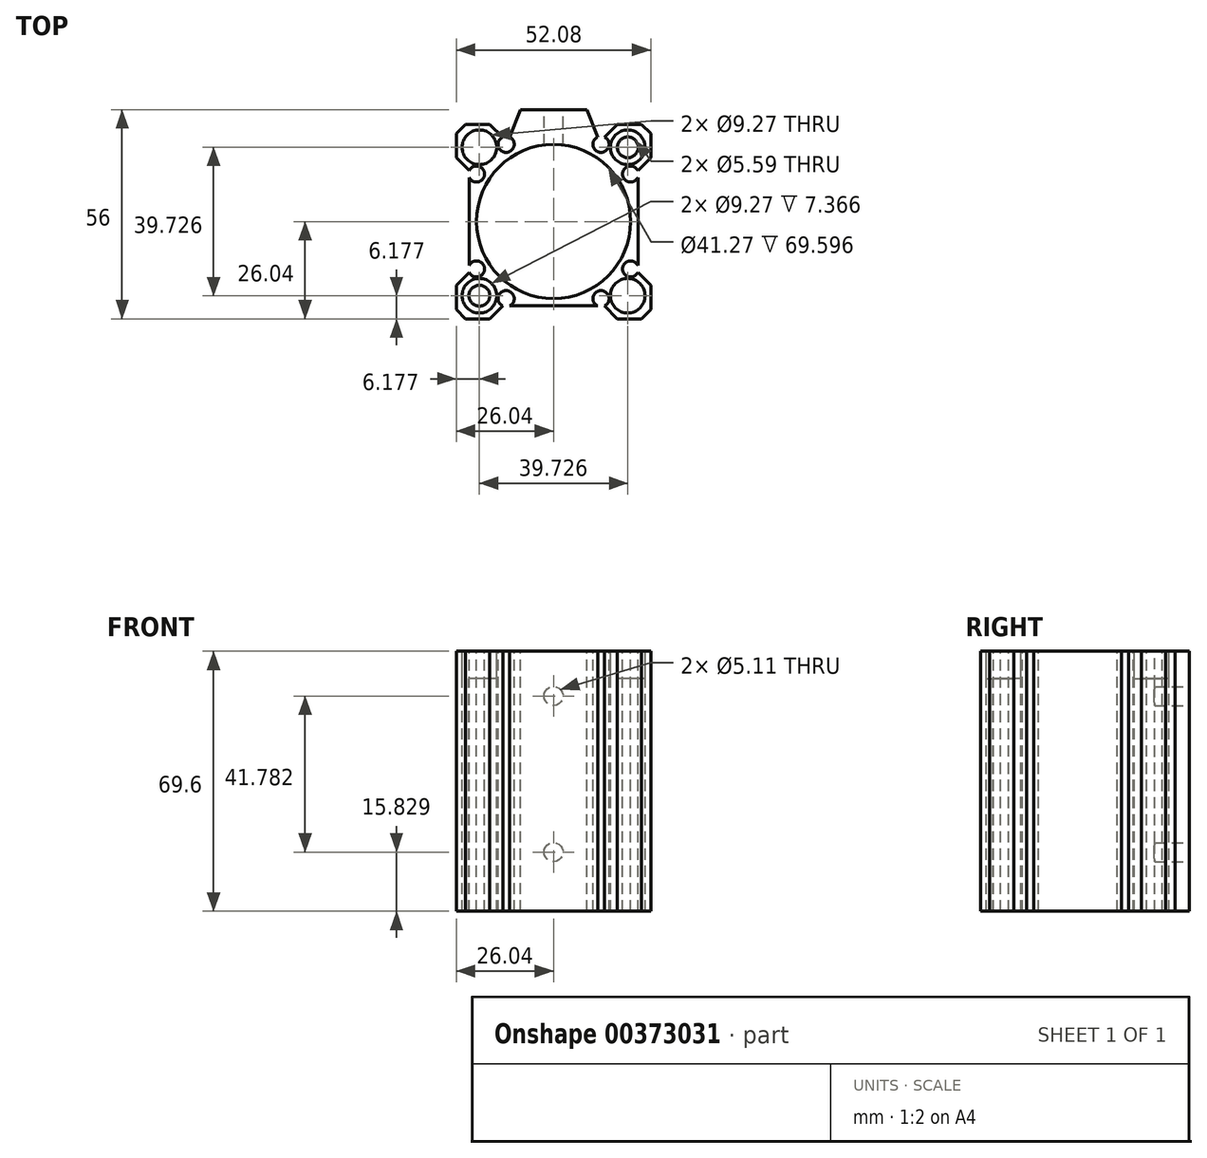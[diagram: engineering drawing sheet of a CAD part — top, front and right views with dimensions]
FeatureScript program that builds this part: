
annotation { "Feature Type Name" : "Feature", "Feature Type Description" : "" }
export const myFeature = defineFeature(function(context is Context, id is Id, definition is map)
    precondition{}
    {
        {
            var Q0;
            Q0=qCreatedBy(makeId("Top.planeOp"),FACE);
            var sketch = newSketch(context, id + "F0", { "sketchPlane" : qUnion([Q0])});
            skLineSegment(sketch, "E0.bottom", {"start": v(23.56, 26.03) * mm, "end": v(17.05, 26.03) * mm});
            skLineSegment(sketch, "E0.top", {"start": v(23.56, -26.04) * mm, "end": v(17.05, -26.04) * mm});
            skLineSegment(sketch, "E0.left", {"start": v(26.04, 23.56) * mm, "end": v(26.04, 17.05) * mm});
            skLineSegment(sketch, "E0.right", {"start": v(-26.04, 23.56) * mm, "end": v(-26.04, 17.05) * mm});
            skPoint(sketch, "E0.middle", {"position": v(0, 0) * mm});
            skLineSegment(sketch, "E1.0", {"start": v(-26.04, 17.05) * mm, "end": v(-22.6, 13.61) * mm});
            skLineSegment(sketch, "E2.0", {"start": v(-17.05, 26.04) * mm, "end": v(-13.61, 22.6) * mm});
            skLineSegment(sketch, "E3.0", {"start": v(17.05, 26.03) * mm, "end": v(13.61, 22.6) * mm});
            skLineSegment(sketch, "E4.0", {"start": v(26.04, 17.05) * mm, "end": v(22.6, 13.61) * mm});
            skCircle(sketch, "E5", {"center": v(19.86, 19.86) * mm, "radius": 4.64 * mm});
            skCircle(sketch, "E6.MirrorC", {"center": v(19.86, -19.86) * mm, "radius": 4.64 * mm});
            skCircle(sketch, "E7.MirrorC", {"center": v(-19.86, 19.86) * mm, "radius": 4.64 * mm});
            skCircle(sketch, "E8.MirrorC", {"center": v(-19.86, -19.86) * mm, "radius": 4.64 * mm});
            skLineSegment(sketch, "E9", {"start": v(0, 22.6) * mm, "end": v(0, 0) * mm});
            skArc(sketch, "E10", {"start": v(11.79, 22.6) * mm, "mid": v(12.7, 18.48) * mm, "end": v(13.61, 22.6) * mm});
            skArc(sketch, "E11", {"start": v(22.6, 13.61) * mm, "mid": v(18.48, 12.7) * mm, "end": v(22.6, 11.79) * mm});
            skArc(sketch, "E12.MirrorC", {"start": v(22.6, -13.61) * mm, "mid": v(18.48, -12.7) * mm, "end": v(22.6, -11.79) * mm});
            skArc(sketch, "E13.MirrorC", {"start": v(11.79, -22.6) * mm, "mid": v(12.7, -18.48) * mm, "end": v(13.61, -22.6) * mm});
            skArc(sketch, "E14.MirrorC", {"start": v(-11.79, 22.6) * mm, "mid": v(-12.7, 18.48) * mm, "end": v(-13.61, 22.6) * mm});
            skArc(sketch, "E15.MirrorC", {"start": v(-22.6, 13.61) * mm, "mid": v(-18.48, 12.7) * mm, "end": v(-22.6, 11.79) * mm});
            skArc(sketch, "E16.MirrorC", {"start": v(-22.6, -13.61) * mm, "mid": v(-18.48, -12.7) * mm, "end": v(-22.6, -11.79) * mm});
            skArc(sketch, "E17.MirrorC", {"start": v(-11.79, -22.6) * mm, "mid": v(-12.7, -18.48) * mm, "end": v(-13.61, -22.6) * mm});
            skLineSegment(sketch, "E18", {"start": v(-23.56, 26.03) * mm, "end": v(-26.04, 23.56) * mm});
            skLineSegment(sketch, "E19", {"start": v(23.56, 26.03) * mm, "end": v(26.04, 23.56) * mm});
            skLineSegment(sketch, "E20", {"start": v(26.04, -23.56) * mm, "end": v(23.56, -26.03) * mm});
            skLineSegment(sketch, "E21", {"start": v(-23.56, -26.03) * mm, "end": v(-26.04, -23.56) * mm});
            skPoint(sketch, "E22.orphan", {"position": v(-26.04, -26.03) * mm});
            skPoint(sketch, "E23.orphan", {"position": v(26.03, -26.04) * mm});
            skPoint(sketch, "E24.orphan", {"position": v(26.04, 26.04) * mm});
            skPoint(sketch, "E25.orphan", {"position": v(-26.04, 26.04) * mm});
            skLineSegment(sketch, "E26.trimOffspring", {"start": v(26.04, -17.05) * mm, "end": v(26.04, -23.56) * mm});
            skLineSegment(sketch, "E27.trimOffspring", {"start": v(-17.05, 26.03) * mm, "end": v(-23.56, 26.03) * mm});
            skPoint(sketch, "E28.orphan", {"position": v(12.7, 26.03) * mm});
            skPoint(sketch, "E29.orphan", {"position": v(-12.7, 26.03) * mm});
            skLineSegment(sketch, "E30.trimOffspring", {"start": v(22.6, -13.61) * mm, "end": v(26.04, -17.05) * mm});
            skLineSegment(sketch, "E31.trimOffspring", {"start": v(13.61, -22.6) * mm, "end": v(17.05, -26.04) * mm});
            skLineSegment(sketch, "E32.trimOffspring", {"start": v(-17.05, -26.04) * mm, "end": v(-23.56, -26.04) * mm});
            skLineSegment(sketch, "E33.trimOffspring", {"start": v(-13.61, -22.6) * mm, "end": v(-17.05, -26.03) * mm});
            skLineSegment(sketch, "E34.trimOffspring", {"start": v(-26.04, -17.05) * mm, "end": v(-26.04, -23.56) * mm});
            skLineSegment(sketch, "E35.trimOffspring", {"start": v(-22.6, -13.61) * mm, "end": v(-26.03, -17.05) * mm});
            skLineSegment(sketch, "E36", {"start": v(-11.79, 22.6) * mm, "end": v(11.79, 22.6) * mm});
            skLineSegment(sketch, "E37", {"start": v(22.6, 11.79) * mm, "end": v(22.6, -11.79) * mm});
            skLineSegment(sketch, "E38", {"start": v(11.79, -22.6) * mm, "end": v(-11.79, -22.6) * mm});
            skLineSegment(sketch, "E39", {"start": v(-22.6, -11.79) * mm, "end": v(-22.6, 11.79) * mm});
            skPoint(sketch, "E40.start.orphan", {"position": v(-26.04, 0) * mm});
            skLineSegment(sketch, "E41.trimOffspring", {"start": v(0, 0) * mm, "end": v(26.04, 0) * mm});
            skPoint(sketch, "E42.trimOffspring.end.orphan", {"position": v(0, -26.03) * mm});
            skCircle(sketch, "E43", {"center": v(0, 0) * mm, "radius": 20.83 * mm});
            skLineSegment(sketch, "E44.0", {"start": v(-8.9, 29.96) * mm, "end": v(8.89, 29.96) * mm});
            skLineSegment(sketch, "E45", {"start": v(0, 26.03) * mm, "end": v(0, 22.6) * mm});
            skLineSegment(sketch, "E46.0", {"start": v(-8.9, 29.96) * mm, "end": v(-8.9, 29.37) * mm});
            skLineSegment(sketch, "E47", {"start": v(-11.79, 22.6) * mm, "end": v(-8.9, 29.96) * mm});
            skLineSegment(sketch, "E48", {"start": v(8.89, 29.96) * mm, "end": v(11.79, 22.6) * mm});
            skPoint(sketch, "E49.orphan", {"position": v(-11.79, 29.96) * mm});
            skPoint(sketch, "E50.orphan", {"position": v(11.79, 29.96) * mm});
            skPoint(sketch, "E51.orphan", {"position": v(0, 29.96) * mm});
            skSolve(sketch);
        }
        {
            var Q0;
            Q0=makeQuery(id+"F0.imprint","IMPRINT",FACE,{"disambiguationData":[TD([[makeQuery(id+"F0.imprint","IMPRINT",EDGE,{"derivedFrom":sQuery(id+"F0.wireOp",EDGE,"E0.top")}),-1.0]])]});
            var Q1;
            Q1=makeQuery(id+"F0.imprint","IMPRINT",FACE,{"disambiguationData":[TD([[makeQuery(id+"F0.imprint","IMPRINT",EDGE,{"derivedFrom":sQuery(id+"F0.wireOp",EDGE,"E44.0")}),-1.0]])]});
            var Q2;
            Q2=makeQuery(id+"F0.imprint","IMPRINT",FACE,{"disambiguationData":[TD([[makeQuery(id+"F0.imprint","IMPRINT",EDGE,{"derivedFrom":sQuery(id+"F0.wireOp",EDGE,"E0.bottom")}),1.0]])]});
            var Q3;
            Q3=makeQuery(id+"F0.imprint","IMPRINT",FACE,{"disambiguationData":[TD([[makeQuery(id+"F0.imprint","IMPRINT",EDGE,{"derivedFrom":sQuery(id+"F0.wireOp",EDGE,"E6.MirrorC")}),-1.0]])]});
            var Q4;
            Q4=makeQuery(id+"F0.imprint","IMPRINT",FACE,{"disambiguationData":[TD([[makeQuery(id+"F0.imprint","IMPRINT",EDGE,{"derivedFrom":sQuery(id+"F0.wireOp",EDGE,"E5")}),1.0]])]});
            var Q5;
            Q5=makeQuery(id+"F0.imprint","IMPRINT",FACE,{"disambiguationData":[TD([[makeQuery(id+"F0.imprint","IMPRINT",EDGE,{"derivedFrom":sQuery(id+"F0.wireOp",EDGE,"E7.MirrorC")}),-1.0]])]});
            var Q6;
            Q6=makeQuery(id+"F0.imprint","IMPRINT",FACE,{"disambiguationData":[TD([[makeQuery(id+"F0.imprint","IMPRINT",EDGE,{"derivedFrom":sQuery(id+"F0.wireOp",EDGE,"E8.MirrorC")}),1.0]])]});
            var Q7;
            {var subQ0=sQuery(id+"F0.wireOp",EDGE,"E41.trimOffspring");var subQ1=sQuery(id+"F0.wireOp",EDGE,"E9");var subQ2=makeQuery(id+"F0.imprint","INTERSECT",VERTEX,{"derivedFrom":[subQ1,subQ0]});Q7=makeQuery(id+"F0.imprint","IMPRINT",FACE,{"disambiguationData":[TD([[makeQuery(id+"F0.imprint","IMPRINT",EDGE,{"disambiguationData":[TD([[subQ2,1.0]])],"derivedFrom":subQ1}),1.0]])]});}
            var Q8;
            {var subQ0=sQuery(id+"F0.wireOp",EDGE,"E41.trimOffspring");var subQ1=sQuery(id+"F0.wireOp",EDGE,"E9");var subQ2=makeQuery(id+"F0.imprint","INTERSECT",VERTEX,{"derivedFrom":[subQ1,subQ0]});Q8=makeQuery(id+"F0.imprint","IMPRINT",FACE,{"disambiguationData":[TD([[makeQuery(id+"F0.imprint","IMPRINT",EDGE,{"disambiguationData":[TD([[subQ2,1.0]])],"derivedFrom":subQ1}),-1.0]])]});}
            extrude(context, id + "F1", {"entities" : qUnion([Q0, Q1, Q2, Q3, Q4, Q5, Q6, Q7, Q8]), "oppositeDirection" : true, "depth" : 69.6 * mm, "offsetDistance" : 25.4 * mm});
        }
        {
            var Q0;
            Q0=sQuery(id+"F0.wireOp",VERTEX,"E7.MirrorC.center");
            var Q1;
            Q1=sQuery(id+"F0.wireOp",VERTEX,"E5.center");
            var Q2;
            Q2=sQuery(id+"F0.wireOp",VERTEX,"E6.MirrorC.center");
            var Q3;
            Q3=sQuery(id+"F0.wireOp",VERTEX,"E8.MirrorC.center");
            var Q4;
            Q4=makeQuery(id+"F1.opExtrude","SWEPT_BODY",BODY,{"disambiguationData":[OSD([sQuery(id+"F0.wireOp",EDGE,"E0.bottom"),sQuery(id+"F0.wireOp",EDGE,"E0.top"),sQuery(id+"F0.wireOp",EDGE,"E0.left"),sQuery(id+"F0.wireOp",EDGE,"E0.right"),sQuery(id+"F0.wireOp",EDGE,"E1.0"),sQuery(id+"F0.wireOp",EDGE,"E2.0"),sQuery(id+"F0.wireOp",EDGE,"E3.0"),sQuery(id+"F0.wireOp",EDGE,"E4.0"),sQuery(id+"F0.wireOp",EDGE,"E10"),sQuery(id+"F0.wireOp",EDGE,"E11"),sQuery(id+"F0.wireOp",EDGE,"E12.MirrorC"),sQuery(id+"F0.wireOp",EDGE,"E13.MirrorC"),sQuery(id+"F0.wireOp",EDGE,"E14.MirrorC"),sQuery(id+"F0.wireOp",EDGE,"E15.MirrorC"),sQuery(id+"F0.wireOp",EDGE,"E16.MirrorC"),sQuery(id+"F0.wireOp",EDGE,"E17.MirrorC"),sQuery(id+"F0.wireOp",EDGE,"E18"),sQuery(id+"F0.wireOp",EDGE,"E19"),sQuery(id+"F0.wireOp",EDGE,"E20"),sQuery(id+"F0.wireOp",EDGE,"E21"),sQuery(id+"F0.wireOp",EDGE,"E26.trimOffspring"),sQuery(id+"F0.wireOp",EDGE,"E27.trimOffspring"),sQuery(id+"F0.wireOp",EDGE,"E30.trimOffspring"),sQuery(id+"F0.wireOp",EDGE,"E31.trimOffspring"),sQuery(id+"F0.wireOp",EDGE,"E32.trimOffspring"),sQuery(id+"F0.wireOp",EDGE,"E33.trimOffspring"),sQuery(id+"F0.wireOp",EDGE,"E34.trimOffspring"),sQuery(id+"F0.wireOp",EDGE,"E35.trimOffspring"),sQuery(id+"F0.wireOp",EDGE,"E37"),sQuery(id+"F0.wireOp",EDGE,"E38"),sQuery(id+"F0.wireOp",EDGE,"E39"),sQuery(id+"F0.wireOp",EDGE,"E44.0"),sQuery(id+"F0.wireOp",EDGE,"E47"),sQuery(id+"F0.wireOp",EDGE,"E48")])]});
            hole(context, id + "F2", {"style" : HoleStyle.C_BORE, "endStyle" : HoleEndStyle.THROUGH, "holeDiameter" : 5.6 * mm, "cBoreDiameter" : 9.27 * mm, "cBoreDepth" : 7.37 * mm, "majorDiameter" : 6.35 * mm, "isTappedThrough" : true, "tappedDepth" : 13.2 * mm, "tapClearance" : 3, "startFromSketch" : true, "locations" : qUnion([Q0, Q1, Q2, Q3]), "scope" : qUnion([Q4])});
        }
        {
            var Q0;
            Q0=sQuery(id+"F0.wireOp",VERTEX,"E0.middle");
            var Q1;
            Q1=makeQuery(id+"F1.opExtrude","SWEPT_BODY",BODY,{"disambiguationData":[OSD([sQuery(id+"F0.wireOp",EDGE,"E0.bottom"),sQuery(id+"F0.wireOp",EDGE,"E0.top"),sQuery(id+"F0.wireOp",EDGE,"E0.left"),sQuery(id+"F0.wireOp",EDGE,"E0.right"),sQuery(id+"F0.wireOp",EDGE,"E1.0"),sQuery(id+"F0.wireOp",EDGE,"E2.0"),sQuery(id+"F0.wireOp",EDGE,"E3.0"),sQuery(id+"F0.wireOp",EDGE,"E4.0"),sQuery(id+"F0.wireOp",EDGE,"E10"),sQuery(id+"F0.wireOp",EDGE,"E11"),sQuery(id+"F0.wireOp",EDGE,"E12.MirrorC"),sQuery(id+"F0.wireOp",EDGE,"E13.MirrorC"),sQuery(id+"F0.wireOp",EDGE,"E14.MirrorC"),sQuery(id+"F0.wireOp",EDGE,"E15.MirrorC"),sQuery(id+"F0.wireOp",EDGE,"E16.MirrorC"),sQuery(id+"F0.wireOp",EDGE,"E17.MirrorC"),sQuery(id+"F0.wireOp",EDGE,"E18"),sQuery(id+"F0.wireOp",EDGE,"E19"),sQuery(id+"F0.wireOp",EDGE,"E20"),sQuery(id+"F0.wireOp",EDGE,"E21"),sQuery(id+"F0.wireOp",EDGE,"E26.trimOffspring"),sQuery(id+"F0.wireOp",EDGE,"E27.trimOffspring"),sQuery(id+"F0.wireOp",EDGE,"E30.trimOffspring"),sQuery(id+"F0.wireOp",EDGE,"E31.trimOffspring"),sQuery(id+"F0.wireOp",EDGE,"E32.trimOffspring"),sQuery(id+"F0.wireOp",EDGE,"E33.trimOffspring"),sQuery(id+"F0.wireOp",EDGE,"E34.trimOffspring"),sQuery(id+"F0.wireOp",EDGE,"E35.trimOffspring"),sQuery(id+"F0.wireOp",EDGE,"E37"),sQuery(id+"F0.wireOp",EDGE,"E38"),sQuery(id+"F0.wireOp",EDGE,"E39"),sQuery(id+"F0.wireOp",EDGE,"E44.0"),sQuery(id+"F0.wireOp",EDGE,"E47"),sQuery(id+"F0.wireOp",EDGE,"E48")])]});
            hole(context, id + "F3", {"style" : HoleStyle.SIMPLE, "endStyle" : HoleEndStyle.THROUGH, "holeDiameter" : 41.27 * mm, "majorDiameter" : 6.35 * mm, "isTappedThrough" : true, "tappedDepth" : 13.2 * mm, "tapClearance" : 3, "startFromSketch" : true, "locations" : qUnion([Q0]), "scope" : qUnion([Q1])});
        }
        {
            var Q0;
            Q0=makeQuery(id+"F1.opExtrude","SWEPT_FACE",FACE,{"disambiguationData":[OSD([sQuery(id+"F0.wireOp",EDGE,"E44.0")])]});
            var sketch = newSketch(context, id + "F4", { "sketchPlane" : qUnion([Q0])});
            skLineSegment(sketch, "E52", {"start": v(0, 0) * mm, "end": v(0, -69.6) * mm});
            skLineSegment(sketch, "E53", {"start": v(-10.34, -11.99) * mm, "end": v(11.12, -11.99) * mm});
            skLineSegment(sketch, "E54", {"start": v(-10.46, -53.77) * mm, "end": v(11.12, -53.77) * mm});
            skPoint(sketch, "E55", {"position": v(0, -11.99) * mm});
            skPoint(sketch, "E56", {"position": v(0, -53.77) * mm});
            skSolve(sketch);
        }
        {
            var Q0;
            Q0=sQuery(id+"F4.wireOp",VERTEX,"E55");
            var Q1;
            Q1=sQuery(id+"F4.wireOp",VERTEX,"E56");
            var Q2;
            Q2=makeQuery(id+"F1.opExtrude","SWEPT_BODY",BODY,{"disambiguationData":[OSD([sQuery(id+"F0.wireOp",EDGE,"E0.bottom"),sQuery(id+"F0.wireOp",EDGE,"E0.top"),sQuery(id+"F0.wireOp",EDGE,"E0.left"),sQuery(id+"F0.wireOp",EDGE,"E0.right"),sQuery(id+"F0.wireOp",EDGE,"E1.0"),sQuery(id+"F0.wireOp",EDGE,"E2.0"),sQuery(id+"F0.wireOp",EDGE,"E3.0"),sQuery(id+"F0.wireOp",EDGE,"E4.0"),sQuery(id+"F0.wireOp",EDGE,"E10"),sQuery(id+"F0.wireOp",EDGE,"E11"),sQuery(id+"F0.wireOp",EDGE,"E12.MirrorC"),sQuery(id+"F0.wireOp",EDGE,"E13.MirrorC"),sQuery(id+"F0.wireOp",EDGE,"E14.MirrorC"),sQuery(id+"F0.wireOp",EDGE,"E15.MirrorC"),sQuery(id+"F0.wireOp",EDGE,"E16.MirrorC"),sQuery(id+"F0.wireOp",EDGE,"E17.MirrorC"),sQuery(id+"F0.wireOp",EDGE,"E18"),sQuery(id+"F0.wireOp",EDGE,"E19"),sQuery(id+"F0.wireOp",EDGE,"E20"),sQuery(id+"F0.wireOp",EDGE,"E21"),sQuery(id+"F0.wireOp",EDGE,"E26.trimOffspring"),sQuery(id+"F0.wireOp",EDGE,"E27.trimOffspring"),sQuery(id+"F0.wireOp",EDGE,"E30.trimOffspring"),sQuery(id+"F0.wireOp",EDGE,"E31.trimOffspring"),sQuery(id+"F0.wireOp",EDGE,"E32.trimOffspring"),sQuery(id+"F0.wireOp",EDGE,"E33.trimOffspring"),sQuery(id+"F0.wireOp",EDGE,"E34.trimOffspring"),sQuery(id+"F0.wireOp",EDGE,"E35.trimOffspring"),sQuery(id+"F0.wireOp",EDGE,"E37"),sQuery(id+"F0.wireOp",EDGE,"E38"),sQuery(id+"F0.wireOp",EDGE,"E39"),sQuery(id+"F0.wireOp",EDGE,"E44.0"),sQuery(id+"F0.wireOp",EDGE,"E47"),sQuery(id+"F0.wireOp",EDGE,"E48")])]});
            hole(context, id + "F5", {"style" : HoleStyle.SIMPLE, "endStyle" : HoleEndStyle.BLIND, "standardTappedOrClearance" : lookupTablePath({ "standard" : "ANSI", "engagement" : "75%", "pitch" : "20 tpi", "size" : "1/4", "type" : "Tapped" }), "standardBlindInLast" : lookupTablePath({ "standard" : "ANSI", "fit" : "Normal", "engagement" : "75%", "pitch" : "20 tpi", "size" : "1/4", "type" : "Clearance & tapped" }), "holeDiameter" : 5.1 * mm, "majorDiameter" : 6.35 * mm, "showTappedDepth" : true, "holeDepth" : 16.51 * mm, "isTappedThrough" : true, "tappedDepth" : 12.7 * mm, "tapClearance" : 3, "startFromSketch" : true, "locations" : qUnion([Q0, Q1]), "scope" : qUnion([Q2])});
        }
    });
